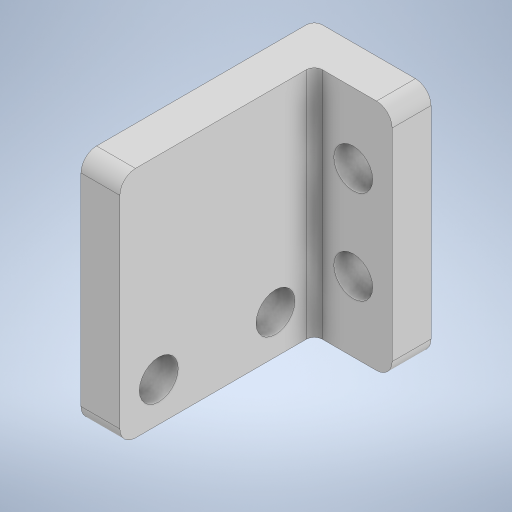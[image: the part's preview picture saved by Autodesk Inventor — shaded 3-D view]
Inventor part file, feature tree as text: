
AUTODESK INVENTOR PART (.ipt)
format: ipt  version: 2024.3 (Build 283343000, 343)  size: 275,456 bytes
history: native  units: mm
features: sketch x5, extrude x3, hole x2, fillet x2, other x1
ambient origin geometry x8: Origin, YZ Plane, XZ Plane, XY Plane, X Axis, Y Axis, Z Axis, Center Point
bodies: Body1 (feature_tree), Body2 (feature_tree)
feature tree (13):
  other  "ソリッド1"
  extrude  "押し出し1"  Depth=30.0mm
  hole  "穴1"  [1 undecoded]
  extrude  "押し出し2"  Depth=30.0mm
  hole  "穴2"  [1 undecoded]
  extrude  "押し出し3"  Depth=5.0mm TaperAngle=0.0deg
  fillet  "フィレット1"  Radius=10.0mm
  fillet  "フィレット2"  Radius=5.0mm
  sketch  "スケッチ1"
  sketch  "スケッチ2"
  sketch  "スケッチ3"
  sketch  "スケッチ4"
  sketch  "スケッチ5"
note: 2 required parameter values undecoded (feature->parameter linkage not recoverable at this tier; creation-order binding heuristic only, values carry confidence <= 0.55)
